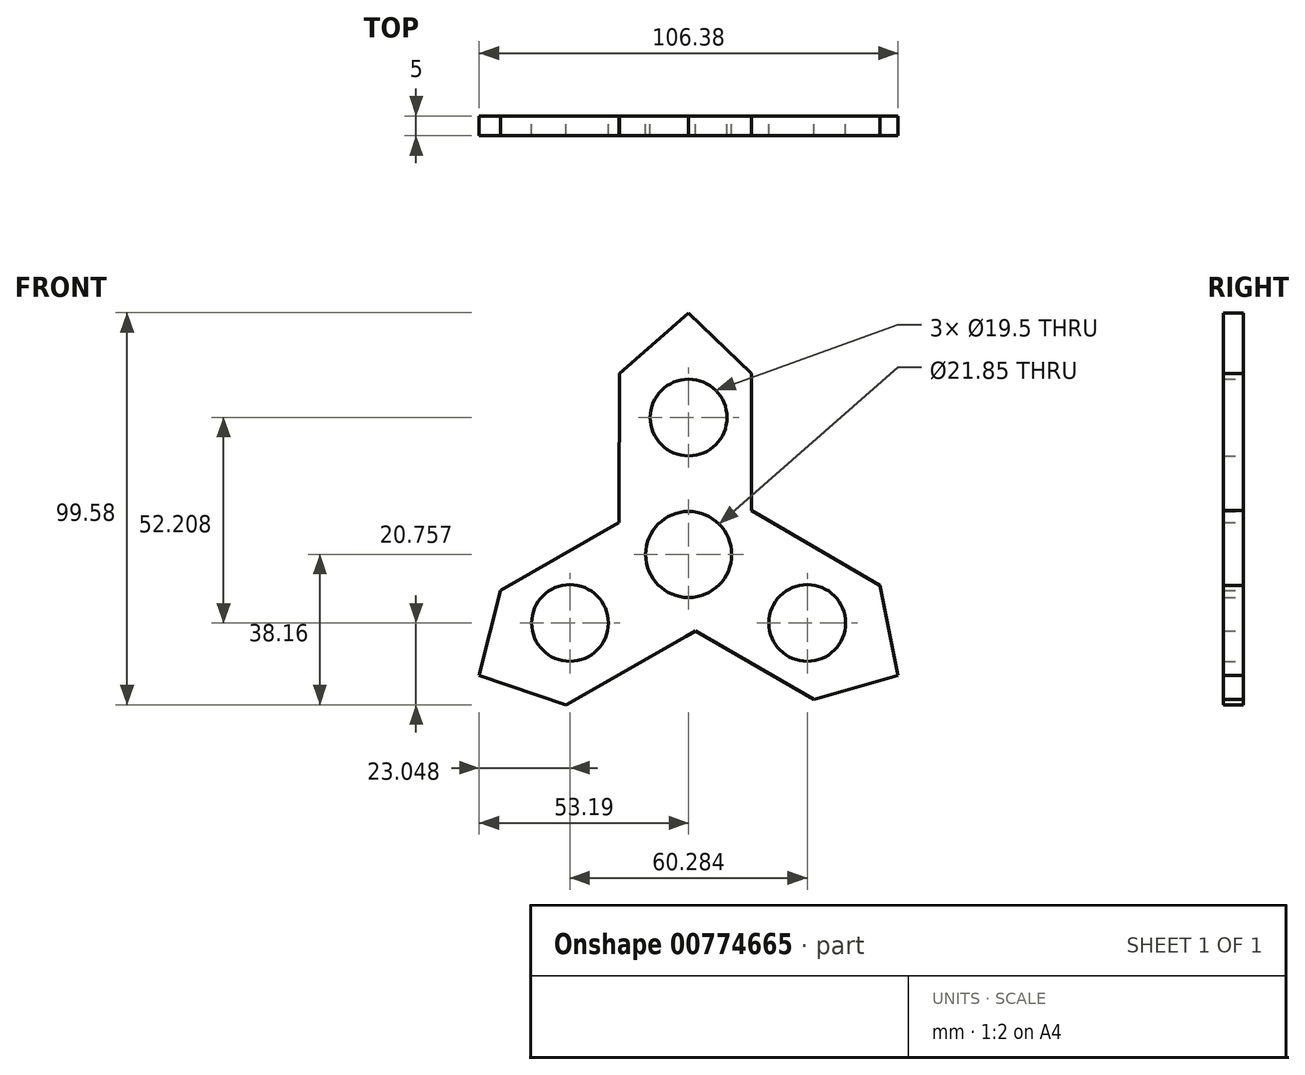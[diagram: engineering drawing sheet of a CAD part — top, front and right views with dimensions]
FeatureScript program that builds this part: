
annotation { "Feature Type Name" : "Feature", "Feature Type Description" : "" }
export const myFeature = defineFeature(function(context is Context, id is Id, definition is map)
    precondition{}
    {
        {
            var Q0;
            Q0=qCreatedBy(makeId("Front.planeOp"),FACE);
            var sketch = newSketch(context, id + "F0", { "sketchPlane" : qUnion([Q0])});
            skCircle(sketch, "E0", {"center": v(0, 0) * mm, "radius": 10.93 * mm});
            skPoint(sketch, "E1.center.orphan", {"position": v(2.4, 29.02) * mm});
            skPoint(sketch, "E2.center.orphan", {"position": v(0, 34.8) * mm});
            skLineSegment(sketch, "E3", {"start": v(-17.68, 11.02) * mm, "end": v(-17.5, 46.02) * mm});
            skLineSegment(sketch, "E4", {"start": v(15.92, 10.93) * mm, "end": v(15.92, 45.93) * mm});
            skLineSegment(sketch, "E5", {"start": v(-17.5, 46.02) * mm, "end": v(0, 61.42) * mm});
            skLineSegment(sketch, "E6", {"start": v(0, 61.42) * mm, "end": v(15.92, 45.93) * mm});
            skCircle(sketch, "E7", {"center": v(0, 34.8) * mm, "radius": 9.75 * mm});
            skLineSegment(sketch, "E8", {"start": v(-17.68, 11.02) * mm, "end": v(-17.68, 8.18) * mm});
            skLineSegment(sketch, "E9.1.0", {"start": v(-31.1, -38.16) * mm, "end": v(-53.19, -30.7) * mm});
            skLineSegment(sketch, "E9.1.1", {"start": v(-53.19, -30.7) * mm, "end": v(-47.73, -9.17) * mm});
            skLineSegment(sketch, "E9.1.2", {"start": v(-17.42, 8.33) * mm, "end": v(-47.73, -9.17) * mm});
            skLineSegment(sketch, "E9.1.3", {"start": v(-0.7, -20.82) * mm, "end": v(-31.1, -38.16) * mm});
            skLineSegment(sketch, "E9.1.4", {"start": v(-0.7, -20.82) * mm, "end": v(1.76, -19.4) * mm});
            skCircle(sketch, "E9.1.6", {"center": v(-30.14, -17.4) * mm, "radius": 9.75 * mm});
            skLineSegment(sketch, "E9.2.0", {"start": v(48.6, -7.85) * mm, "end": v(53.19, -30.7) * mm});
            skLineSegment(sketch, "E9.2.1", {"start": v(53.19, -30.7) * mm, "end": v(31.81, -36.75) * mm});
            skLineSegment(sketch, "E9.2.2", {"start": v(1.5, -19.25) * mm, "end": v(31.81, -36.75) * mm});
            skLineSegment(sketch, "E9.2.3", {"start": v(18.38, 9.8) * mm, "end": v(48.6, -7.85) * mm});
            skLineSegment(sketch, "E9.2.4", {"start": v(18.38, 9.8) * mm, "end": v(15.92, 11.23) * mm});
            skCircle(sketch, "E9.2.6", {"center": v(30.14, -17.4) * mm, "radius": 9.75 * mm});
            skSolve(sketch);
        }
        {
            var Q0;
            Q0 = qSketchRegion(id + "F0", true);
            extrude(context, id + "F1", {"entities" : qUnion([Q0]), "depth" : 5 * mm, "offsetDistance" : 25 * mm});
        }
    });
